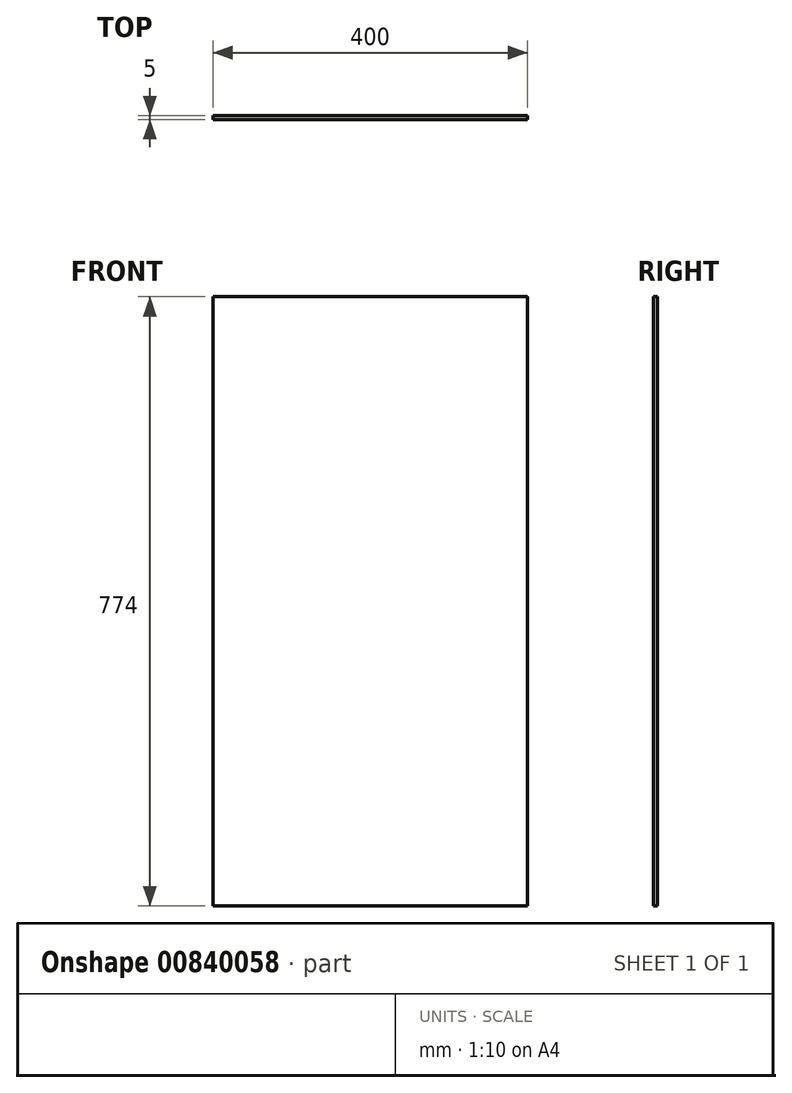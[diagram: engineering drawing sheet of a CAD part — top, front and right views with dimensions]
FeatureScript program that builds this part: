
annotation { "Feature Type Name" : "Feature", "Feature Type Description" : "" }
export const myFeature = defineFeature(function(context is Context, id is Id, definition is map)
    precondition{}
    {
        {
            var Q0;
            Q0=qCreatedBy(makeId("Front.planeOp"),FACE);
            var sketch = newSketch(context, id + "F0", { "sketchPlane" : qUnion([Q0])});
            skLineSegment(sketch, "E0.bottom", {"start": v(-200, 387) * mm, "end": v(200, 387) * mm});
            skLineSegment(sketch, "E0.top", {"start": v(-200, -387) * mm, "end": v(200, -387) * mm});
            skLineSegment(sketch, "E0.left", {"start": v(-200, 387) * mm, "end": v(-200, -387) * mm});
            skLineSegment(sketch, "E0.right", {"start": v(200, 387) * mm, "end": v(200, -387) * mm});
            skSolve(sketch);
        }
        {
            var Q0;
            Q0=makeQuery(id+"F0.imprint","IMPRINT",FACE,{"disambiguationData":[TD([[makeQuery(id+"F0.imprint","IMPRINT",EDGE,{"derivedFrom":sQuery(id+"F0.wireOp",EDGE,"E0.bottom")}),-1.0]])]});
            extrude(context, id + "F1", {"entities" : qUnion([Q0]), "endBound" : BoundingType.SYMMETRIC, "depth" : 5 * mm, "offsetDistance" : 25 * mm});
        }
    });
